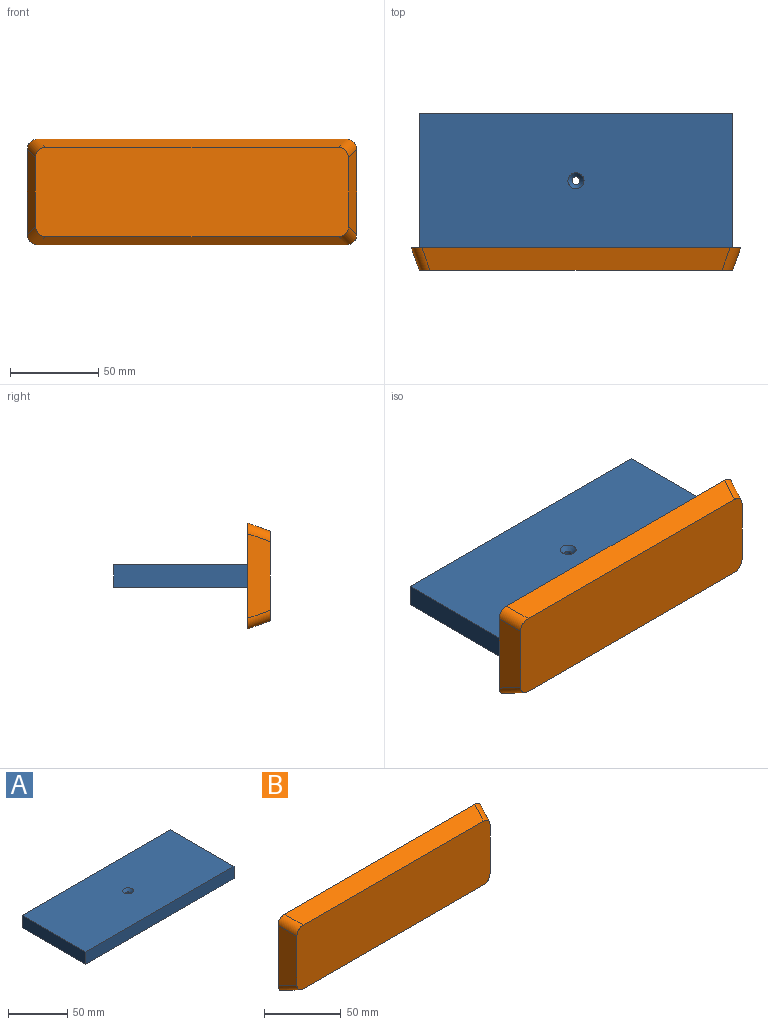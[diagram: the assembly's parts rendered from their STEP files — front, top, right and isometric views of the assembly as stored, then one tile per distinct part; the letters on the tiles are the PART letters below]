
ASSEMBLY  parts=2 mates=1
PART A: 8 faces, bbox 177.8x76.2x12.7 mm
  f0: plane 177.8x12.7mm, normal (0,1,0), area 2258.1mm2, adj f1,f3,f4,f5
  f1: plane 76.2x12.7mm, normal (-1,0,0), area 967.7mm2, adj f0,f2,f4,f5
  f2: plane 177.8x12.7mm, normal (0,-1,0), area 2258.1mm2, adj f1,f3,f4,f5
  f3: plane 76.2x12.7mm, normal (1,0,0), area 967.7mm2, adj f0,f2,f4,f5
  f4: plane 177.8x76.2mm, normal (0,0,1), area 13483.1mm2, adj f0,f1,f2,f3,f7
  f5: plane 177.8x76.2mm, normal (0,0,-1), area 13532.5mm2, adj f0,f1,f2,f3,f6
  f6: cylinder r=2.25mm len=10.04mm, axis (0,0,1), area 141.8mm2, adj f5,f7
  f7: cone r=2.25mm half-angle=41deg, axis (0,0,1), area 75.3mm2, adj f4,f6
PART B: 19 faces, bbox 187.6x14.2x60.6 mm
  f0: plane 187.05x60.05mm, normal (0,1,0), area 1602mm2, adj f1,f2,f3,f4,f6,f7,f8,f9
  f1: plane 175.11x12.7mm, normal (0,-0.34,0.94), area 2304.2mm2, adj f0,f5,f6,f9
  f2: plane 48.11x12.7mm, normal (-0.94,-0.34,0), area 587.7mm2, adj f0,f5,f6,f7
  f3: plane 175.11x12.7mm, normal (0,-0.34,-0.94), area 2304.2mm2, adj f0,f5,f7,f8
  f4: plane 48.11x12.7mm, normal (0.94,-0.34,0), area 587.7mm2, adj f0,f5,f8,f9
  f5: plane 177.8x50.8mm, normal (0,-1,0), area 9002.8mm2, adj f1,f2,f3,f4,f6,f7,f8,f9
  f6: cylinder r=6.35mm len=14.17mm, axis (-0.32,0.89,0.32), area 131.8mm2, adj f0,f1,f2,f5
  f7: cylinder r=6.35mm len=14.17mm, axis (-0.32,0.89,-0.32), area 131.8mm2, adj f0,f2,f3,f5
  f8: cylinder r=6.35mm len=14.17mm, axis (0.32,0.89,-0.32), area 131.8mm2, adj f0,f3,f4,f5
  f9: cylinder r=6.35mm len=14.17mm, axis (0.32,0.89,0.32), area 131.8mm2, adj f0,f1,f4,f5
  f10: plane 174.32x9.53mm, normal (0,0.34,-0.94), area 1731.8mm2, adj f0,f14,f15,f18
  f11: plane 47.32x9.53mm, normal (0.94,0.34,0), area 444.5mm2, adj f0,f14,f15,f16
  f12: plane 174.32x9.53mm, normal (0,0.34,0.94), area 1731.8mm2, adj f0,f14,f16,f17
  f13: plane 47.32x9.53mm, normal (-0.94,0.34,0), area 444.5mm2, adj f0,f14,f17,f18
  f14: plane 173.35x46.35mm, normal (0,1,0), area 8028.2mm2, adj f10,f11,f12,f13,f15,f16,f17,f18
  f15: cylinder r=3.17mm len=10.26mm, axis (-0.32,0.89,0.32), area 49.4mm2, adj f0,f10,f11,f14
  f16: cylinder r=3.17mm len=10.26mm, axis (-0.32,0.89,-0.32), area 49.4mm2, adj f0,f11,f12,f14
  f17: cylinder r=3.17mm len=10.26mm, axis (0.32,0.89,-0.32), area 49.4mm2, adj f0,f12,f13,f14
  f18: cylinder r=3.17mm len=10.26mm, axis (0.32,0.89,0.32), area 49.4mm2, adj f0,f10,f13,f14
PLACE A at identity fixed
PLACE B t=(0,-38.1,6.35)mm
MATE planar B.f0 <-> A.f2  axis (0,1,0) through (0,-38.1,6.35)mm
